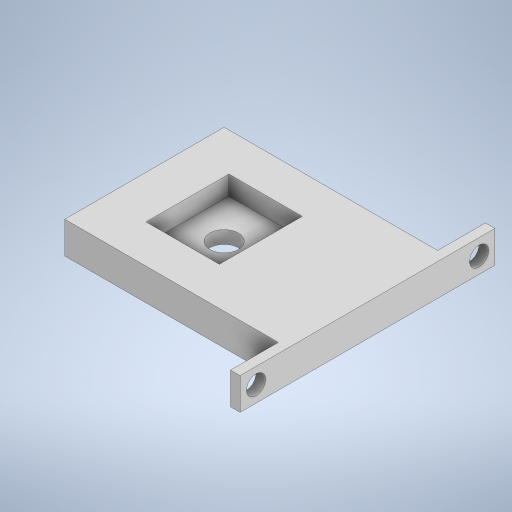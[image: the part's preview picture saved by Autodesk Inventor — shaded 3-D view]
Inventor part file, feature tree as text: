
AUTODESK INVENTOR PART (.ipt)
format: ipt  version: 2023 (Build 270158000, 158)  size: 281,088 bytes
history: native  units: mm
features: extrude x3, sketch x3, other x1
ambient origin geometry x8: Origin, YZ Plane, XZ Plane, XY Plane, X Axis, Y Axis, Z Axis, Center Point
bodies: Body1 (feature_tree)
feature tree (7):
  other  "Твердое тело1"
  extrude  "Выдавливание1"  Depth=70.0mm
  extrude  "Выдавливание2"  Depth=50.0mm
  extrude  "Выдавливание4"  Depth=45.0mm
  sketch  "Эскиз1"
  sketch  "Эскиз2"
  sketch  "Эскиз4"
